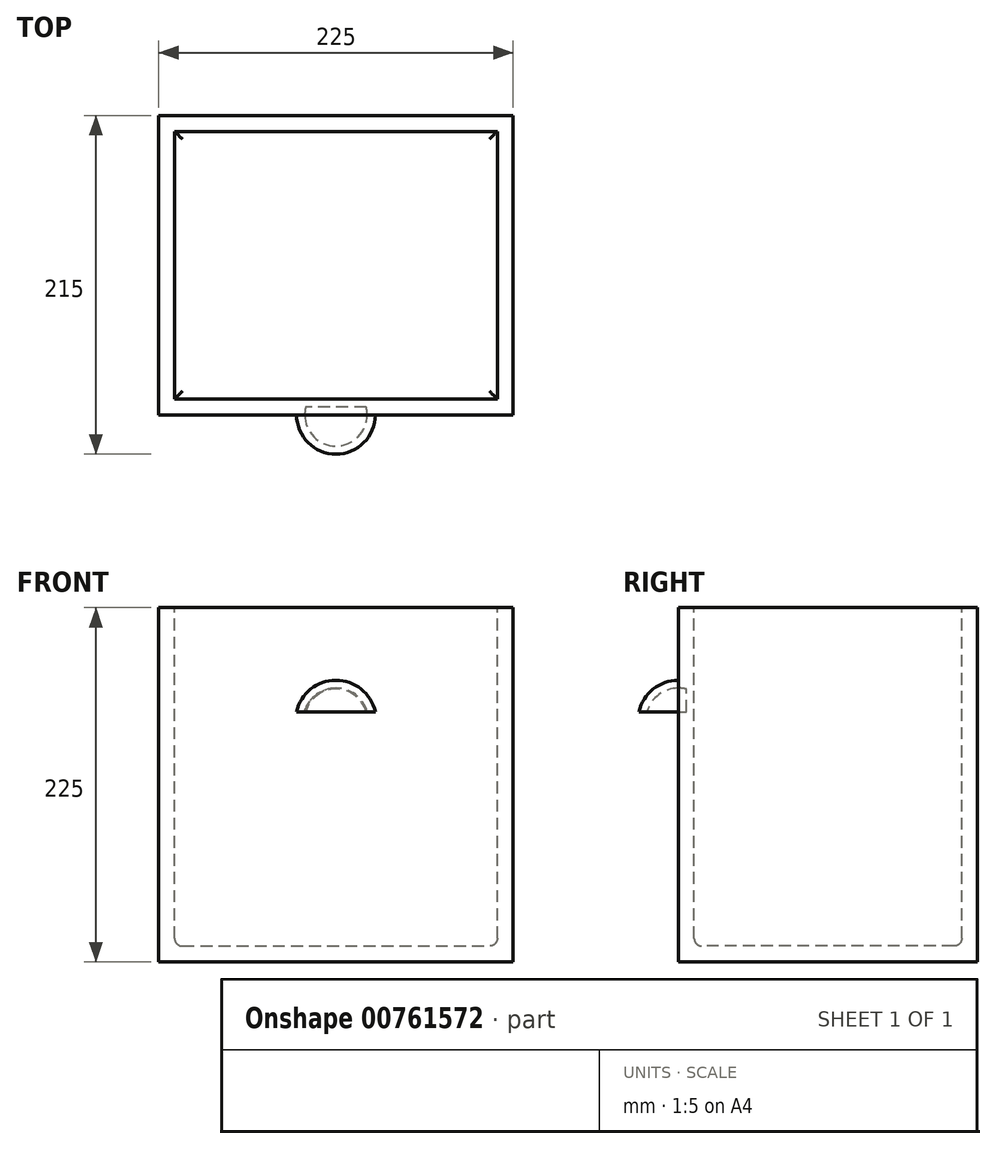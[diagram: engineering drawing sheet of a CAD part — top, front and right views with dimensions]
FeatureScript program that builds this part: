
annotation { "Feature Type Name" : "Feature", "Feature Type Description" : "" }
export const myFeature = defineFeature(function(context is Context, id is Id, definition is map)
    precondition{}
    {
        {
            var Q0;
            Q0=qCreatedBy(makeId("Top.planeOp"),FACE);
            var sketch = newSketch(context, id + "F0", { "sketchPlane" : qUnion([Q0])});
            skLineSegment(sketch, "E0.bottom", {"start": v(-112.5, 190) * mm, "end": v(112.5, 190) * mm});
            skLineSegment(sketch, "E0.top", {"start": v(-112.5, 0) * mm, "end": v(112.5, 0) * mm});
            skLineSegment(sketch, "E0.left", {"start": v(-112.5, 190) * mm, "end": v(-112.5, 0) * mm});
            skLineSegment(sketch, "E0.right", {"start": v(112.5, 190) * mm, "end": v(112.5, 0) * mm});
            skSolve(sketch);
        }
        {
            var Q0;
            Q0=makeQuery(id+"F0.imprint","IMPRINT",FACE,{"disambiguationData":[TD([[makeQuery(id+"F0.imprint","IMPRINT",EDGE,{"derivedFrom":sQuery(id+"F0.wireOp",EDGE,"E0.bottom")}),-1.0]])]});
            extrude(context, id + "F1", {"entities" : qUnion([Q0]), "oppositeDirection" : true, "depth" : 225 * mm, "offsetDistance" : 25 * mm});
        }
        {
            var Q0;
            Q0=makeQuery(id+"F1.opExtrude","CAP_FACE",FACE,{"disambiguationData":[OSD([sQuery(id+"F0.wireOp",EDGE,"E0.bottom"),sQuery(id+"F0.wireOp",EDGE,"E0.top"),sQuery(id+"F0.wireOp",EDGE,"E0.left"),sQuery(id+"F0.wireOp",EDGE,"E0.right")])],"isStart":true});
            shell(context, id + "F2", {"entities" : qUnion([Q0]), "thickness" : 10 * mm});
        }
        {
            var Q0;
            Q0=qCreatedBy(makeId("Front.planeOp"),FACE);
            var sketch = newSketch(context, id + "F3", { "sketchPlane" : qUnion([Q0])});
            skLineSegment(sketch, "E1", {"start": v(0, -46.12) * mm, "end": v(0, -66.12) * mm});
            skLineSegment(sketch, "E2", {"start": v(0, -66.12) * mm, "end": v(25, -66.12) * mm});
            skArc(sketch, "E3", {"start": v(25, -66.12) * mm, "mid": v(16, -51.73) * mm, "end": v(0, -46.12) * mm});
            skSolve(sketch);
        }
        {
            var Q0;
            Q0=makeQuery(id+"F3.imprint","IMPRINT",FACE,{"disambiguationData":[TD([[makeQuery(id+"F3.imprint","IMPRINT",EDGE,{"derivedFrom":sQuery(id+"F3.wireOp",EDGE,"E1")}),1.0]])]});
            var Q1;
            Q1=sQuery(id+"F3.wireOp",EDGE,"E1");
            revolve(context, id + "F4", {"operationType" : NewBodyOperationType.ADD, "surfaceOperationType" : NewSurfaceOperationType.NEW, "entities" : qUnion([Q0]), "axis" : qUnion([Q1]), "revolveType" : RevolveType.ONE_DIRECTION, "angle" : 180 * degree});
        }
        {
            var Q0;
            Q0=makeQuery(id+"F4.opRevolve","SWEPT_FACE",FACE,{"disambiguationData":[OSD([sQuery(id+"F3.wireOp",EDGE,"E2")])]});
            shell(context, id + "F5", {"entities" : qUnion([Q0]), "thickness" : 5 * mm});
        }
        {
            var Q0;
            Q0=makeQuery(id+"F2.opShell","OFFSET_FACE",FACE,{"disambiguationData":[OSD([sQuery(id+"F0.wireOp",EDGE,"E0.bottom"),sQuery(id+"F0.wireOp",EDGE,"E0.top"),sQuery(id+"F0.wireOp",EDGE,"E0.left"),sQuery(id+"F0.wireOp",EDGE,"E0.right")])]});
            fillet(context, id + "F6", {"entities" : qUnion([Q0]), "radius" : 5 * mm, "tangentPropagation" : true, "allowEdgeOverflow" : false});
        }
    });
